# Revit family: Indre By 61118-S
name_source: partatom
category: Meble
units: mm (PartAtom-declared; Revit-internal decimal feet)

## family parameters
Numer OmniClass = 23.40.20.00
Oparty na płaszczyźnie roboczej = Nie
Punkt obliczania pomieszczeń = Nie
Tnij formami wycięć po wczytaniu = Nie
Tytuł OmniClass = General Furniture and Specialties
Współdzielony = Nie
Zawsze pionowo = Tak

## types (1)
- 61118-S
    Domyślna rzędna = 0 mm  [stored 0 ft]
    Height = 80 cm
    Hosted on larslaj.com = https://larslaj.com
    Kobenhagen Materials = larslaj.com/bim
    Lenght = 40 cm
    Maintenance = We recommend to examine and tighten all screws and bolt clamps after a few weeks’ use. In order to prevent cracks and to extend the life of the wood, it is recommended that the wood details should be oiled every 3-5 years.
    Material = Powder coated steel
    Model = 61118-S
    Opis = Indre By Bicycle Stand 40 cm
    Producent = Lars Laj
    Product Groups = Bicycle Stands
    Product line = Indre By
    URL = https://kobenhagen.com
    Weight = 15 kg
    Width = 6 cm
    metal = Kobenhagen RAL 5011

note: [stored X ft] marks values corroborated as IEEE doubles in the binary element streams (Revit-internal decimal feet)
